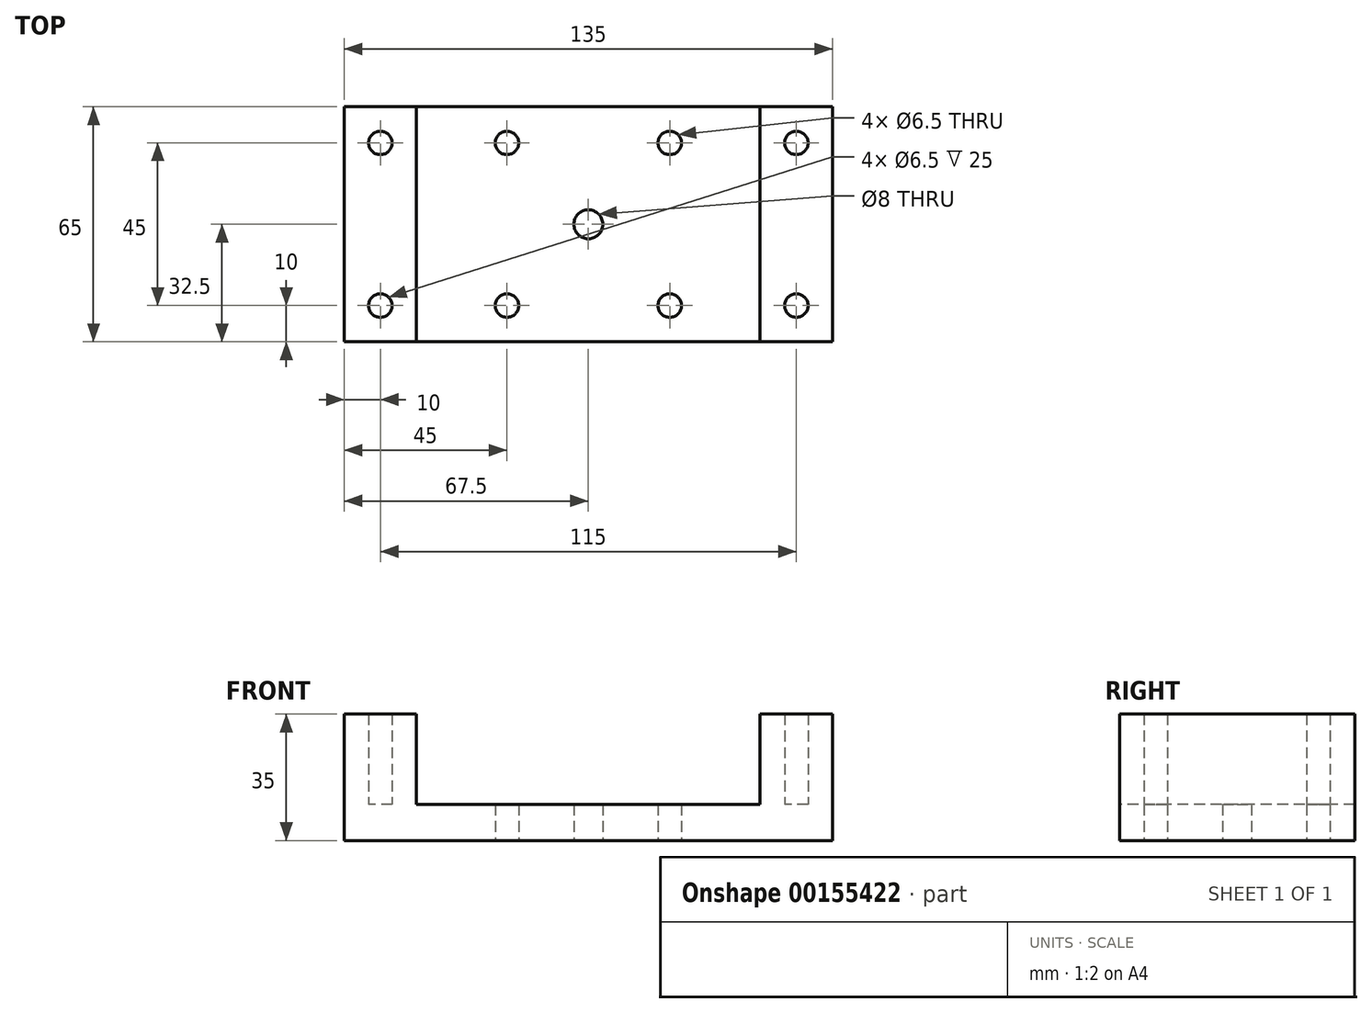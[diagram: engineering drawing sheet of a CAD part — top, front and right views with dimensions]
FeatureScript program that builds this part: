
annotation { "Feature Type Name" : "Feature", "Feature Type Description" : "" }
export const myFeature = defineFeature(function(context is Context, id is Id, definition is map)
    precondition{}
    {
        {
            var Q0;
            Q0=qCreatedBy(makeId("Top.planeOp"),FACE);
            var sketch = newSketch(context, id + "F0", { "sketchPlane" : qUnion([Q0])});
            skLineSegment(sketch, "E0.bottom", {"start": v(67.5, -32.5) * mm, "end": v(-67.5, -32.5) * mm});
            skLineSegment(sketch, "E0.top", {"start": v(67.5, 32.5) * mm, "end": v(-67.5, 32.5) * mm});
            skLineSegment(sketch, "E0.left", {"start": v(67.5, -32.5) * mm, "end": v(67.5, 32.5) * mm});
            skLineSegment(sketch, "E0.right", {"start": v(-67.5, -32.5) * mm, "end": v(-67.5, 32.5) * mm});
            skPoint(sketch, "E0.middle", {"position": v(0, 0) * mm});
            skLineSegment(sketch, "E1.bottom", {"start": v(22.5, -22.5) * mm, "end": v(-22.5, -22.5) * mm, "construction": true});
            skLineSegment(sketch, "E1.top", {"start": v(22.5, 22.5) * mm, "end": v(-22.5, 22.5) * mm, "construction": true});
            skLineSegment(sketch, "E1.left", {"start": v(22.5, -22.5) * mm, "end": v(22.5, 22.5) * mm, "construction": true});
            skLineSegment(sketch, "E1.right", {"start": v(-22.5, -22.5) * mm, "end": v(-22.5, 22.5) * mm, "construction": true});
            skLineSegment(sketch, "E2", {"start": v(-22.5, 22.5) * mm, "end": v(22.5, -22.5) * mm, "construction": true});
            skLineSegment(sketch, "E3", {"start": v(-22.5, -22.5) * mm, "end": v(22.5, 22.5) * mm, "construction": true});
            skCircle(sketch, "E4", {"center": v(-22.5, 22.5) * mm, "radius": 3.25 * mm});
            skCircle(sketch, "E5.MirrorC", {"center": v(22.5, 22.5) * mm, "radius": 3.25 * mm});
            skCircle(sketch, "E6.MirrorC", {"center": v(-22.5, -22.5) * mm, "radius": 3.25 * mm});
            skCircle(sketch, "E7.MirrorC", {"center": v(22.5, -22.5) * mm, "radius": 3.25 * mm});
            skCircle(sketch, "E8", {"center": v(0, 0) * mm, "radius": 4 * mm});
            skSolve(sketch);
        }
        {
            var Q0;
            Q0=makeQuery(id+"F0.imprint","IMPRINT",FACE,{"disambiguationData":[TD([[makeQuery(id+"F0.imprint","IMPRINT",EDGE,{"derivedFrom":sQuery(id+"F0.wireOp",EDGE,"E0.bottom")}),-1.0]])]});
            extrude(context, id + "F1", {"entities" : qUnion([Q0]), "depth" : 10 * mm});
        }
        {
            var Q0;
            Q0=makeQuery(id+"F1.opExtrude","CAP_FACE",FACE,{"disambiguationData":[OSD([sQuery(id+"F0.wireOp",EDGE,"E0.bottom"),sQuery(id+"F0.wireOp",EDGE,"E0.top"),sQuery(id+"F0.wireOp",EDGE,"E0.left"),sQuery(id+"F0.wireOp",EDGE,"E0.right"),sQuery(id+"F0.wireOp",EDGE,"E4"),sQuery(id+"F0.wireOp",EDGE,"E5.MirrorC"),sQuery(id+"F0.wireOp",EDGE,"E6.MirrorC"),sQuery(id+"F0.wireOp",EDGE,"E7.MirrorC"),sQuery(id+"F0.wireOp",EDGE,"E8")])],"isStart":false});
            var sketch = newSketch(context, id + "F2", { "sketchPlane" : qUnion([Q0])});
            skLineSegment(sketch, "E9.bottom", {"start": v(67.5, 32.5) * mm, "end": v(47.5, 32.5) * mm});
            skLineSegment(sketch, "E9.top", {"start": v(67.5, -32.5) * mm, "end": v(47.5, -32.5) * mm});
            skLineSegment(sketch, "E9.left", {"start": v(67.5, 32.5) * mm, "end": v(67.5, -32.5) * mm});
            skLineSegment(sketch, "E9.right", {"start": v(47.5, 32.5) * mm, "end": v(47.5, -32.5) * mm});
            skLineSegment(sketch, "E10.MirrorCS", {"start": v(-67.5, 32.5) * mm, "end": v(-47.5, 32.5) * mm});
            skLineSegment(sketch, "E11.MirrorCS", {"start": v(-47.5, 32.5) * mm, "end": v(-47.5, -32.5) * mm});
            skLineSegment(sketch, "E12.MirrorCS", {"start": v(-67.5, -32.5) * mm, "end": v(-47.5, -32.5) * mm});
            skLineSegment(sketch, "E13.MirrorCS", {"start": v(-67.5, 32.5) * mm, "end": v(-67.5, -32.5) * mm});
            skLineSegment(sketch, "E14", {"start": v(-22.5, 22.5) * mm, "end": v(77.65, 22.5) * mm, "construction": true});
            skCircle(sketch, "E15", {"center": v(57.5, 22.5) * mm, "radius": 3.25 * mm});
            skCircle(sketch, "E16.MirrorC", {"center": v(-57.5, 22.5) * mm, "radius": 3.25 * mm});
            skCircle(sketch, "E17.MirrorC", {"center": v(57.5, -22.5) * mm, "radius": 3.25 * mm});
            skCircle(sketch, "E18.MirrorC", {"center": v(-57.5, -22.5) * mm, "radius": 3.25 * mm});
            skSolve(sketch);
        }
        {
            var Q0;
            Q0 = qSketchRegion(id + "F2", true);
            extrude(context, id + "F3", {"entities" : qUnion([Q0]), "operationType" : NewBodyOperationType.ADD, "depth" : 25 * mm});
        }
    });
